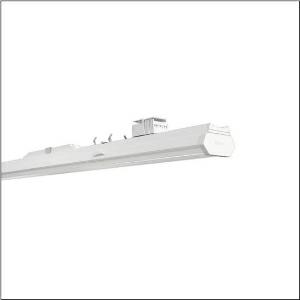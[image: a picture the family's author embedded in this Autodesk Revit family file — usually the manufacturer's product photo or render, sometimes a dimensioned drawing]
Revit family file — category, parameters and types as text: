
# Revit family: licross_r__21_protected_ho_52tp11dn4e5s_2e66
name_source: partatom
category: Lighting Fixtures
units: mm (PartAtom-declared; Revit-internal decimal feet)

## family parameters
Cut with Voids When Loaded = No
Host = Face
Light Source = No
Part Type = Normal
Room Calculation Point = No
Round Connector Dimension = Use Diameter
Shared = No

## types (1)
- --- (1 x LED, 14920 lm, 84.9 W, 4000K)
    Apparent Load = 85 VA
    CIE Flux Codes = 84 94 98 99 100
    Color Rendering = 80
    Color Temperature = 4000K
    Default Elevation = 1800 mm
    Description = Licross® 21 Protected HO, luminaire insert, of sheet steel, galvanised, coil coated, white, length: 1.500mm, width: 90mm, height: 103mm, LED rated luminous flux: 14.920lm, light colour: 840, control gear: DALI 2, with plug, 5-pole, with phase selection, mains connection: 220..240V, AC, 50/60Hz, rated input power: 85W, halogen-free wiring, primary light control with lens, of plastic, primary optical cover: cover, of PMMA, light emission: direct distribution, primary light characteristic: symmetric, protection rating (complete): IP64, insulation class (complete): insulation class I (protective earthing), certification: CE, ENEC, VDE, UKCA, protection symbol: D if used in an environment with conductive dust loads with corresponding accessories, impact resistance: IK06, permissible ambient temperature for indoor applications: -25..+35°C, corresponds to IFS (International Featured Standards) requirements for safety and quality in the food industry, reducing of maximum allowable ambient temperature of 5°C with ceiling mounting, LABS conformity tested according to VDMA 24364:2018-05, packaging unit: 1 piece
    Height = 92 mm
    Lamp = 1 x LED
    Lamp Light Flux = 14920 lm
    Lamp Power = 84.9 W
    Lamp count = 1
    Length = 1500 mm
    Luminous efficacy = 176 lm/W
    Manufacturer = Siteco
    ModVariant = No
    Model = 52TP11DN4E5S
    Mounting Place = Ceiling
    Mounting Type = Pendant
    Number of Poles = 1
    OnlyDefault = Yes
    Power Factor = 1
    Product Name = Licross® 21 Protected HO
    Product group = luminaire insert
    ProductGroupID = 902
    Protection Class = Protection class I
    Protection Degree = IP 64
    RLX_Detail_Level = 1
    RLX_Emergency_Light_Flux = 0 lm
    RLX_Emergency_Type = 0
    RLX_Emergency_Type_DB = No
    RlxData = <blob elided: 24405 chars, md5=2cc8eadb>
    Socket = socket
    Standby Power = 0 W
    System Light Flux = 14920 lm
    System Power = 85 W
    Type Comments = factory setting: luminous flux: 100 % | dim-lin: 254 | 484 mA
    Type Image = l_1256148.jpg
    URL = http://relux.com
    VarID = @adj_128424
    Voltage = 0 V
    Weight = 0.00 kg
    Width = 88 mm

## geometry (parser evidence)
native form markers: Blend x4, Sweep x11
no freeform markers — native parametric forms only
